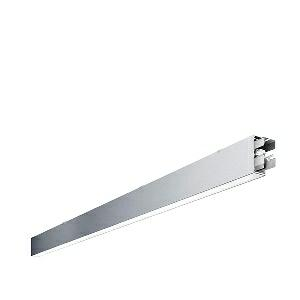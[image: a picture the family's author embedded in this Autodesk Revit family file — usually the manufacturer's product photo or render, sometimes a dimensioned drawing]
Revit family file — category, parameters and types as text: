
# Revit family: dotoo_line_-_dla_3000_830_d_sta_00807970_7aef
name_source: partatom
category: Lighting Fixtures
units: mm (PartAtom-declared; Revit-internal decimal feet)

## family parameters
Cut with Voids When Loaded = No
Host = Face
Light Source = No
Part Type = Normal
Room Calculation Point = No
Round Connector Dimension = Use Diameter
Shared = No

## types (1)
- DOTOO.line - DLA 3000/830/D STA (1 x LED, 2650 lm, 3000K)
    Apparent Load = 26 VA
    Approval mark = CE
    CIE Flux Codes = 67 91 98 100 100
    Color Rendering = 80-89
    Color Temperature = 3000K
    Control Gear = Electronic ballast
    Default Elevation = 1800 mm
    Description = DLA 3000/830/D|Surface-mounted luminaire.|light source: LED|work equipment: Adjustable electronic ballast, digital DALI|connected load: 220-240 V, 50/60 Hz|Power consumption: approx. 26 W|luminous flux: 2650 lm|luminous efficacy: 101 lm/W|light distribution: Direct|colour temperature: Warm white, ca. 3000 K|class of protection: I|technology: Continuously dimmable|mains lead: Connector|glare control: Prism aperture|special features: DALI Load 1x, TouchDIM - dimming via standard switch, Through-wired, up to 18 m on one mains connection, Flicker-free, Suitable as emergency lighting, Start luminaire with mains connection, Mechanical and electrical connection of the individual modules without tools|
    Frequency = 50 Hz
    Height = 110 mm
    Lamp = 1 x LED
    Lamp Light Flux = 2650 lm
    Lamp count = 1
    Length = 2250 mm
    Luminous efficacy = 102 lm/W
    Manufacturer = Waldmann
    ModVariant = No
    Model = 00807970
    Mounting Place = Ceiling
    Mounting Type = Surface mounted
    Number of Poles = 1
    OnlyDefault = Yes
    Power Factor = 1
    Product Name = DOTOO.line - DLA 3000/830/D STA
    Product group = Ceiling mounted luminaire
    ProductGroupID = 3
    Protection Class = Protection class I
    Protection Degree = IP 40
    RLX_Detail_Level = 1
    RLX_Emergency_Light_Flux = 0 lm
    RLX_Emergency_Type = 0
    RLX_Emergency_Type_DB = No
    RlxData = <blob elided: 22721 chars, md5=22592655>
    Socket = socket
    Standby Power = 0 W
    System Light Flux = 2650 lm
    System Power = 26 W
    Type Comments = Product without accessories
    Type Image = 114381000-00807958.jpg
    URL = http://relux.com
    VarID = ---
    Voltage = 230 V
    Voltage Range = 220-240 V
    Weight = 0.00 kg
    Width = 60 mm  [stored 0.19685 ft]

note: [stored X ft] marks values corroborated as IEEE doubles in the binary element streams (Revit-internal decimal feet)

## geometry (parser evidence)
native form markers: Blend x4, Sweep x12
no freeform markers — native parametric forms only
